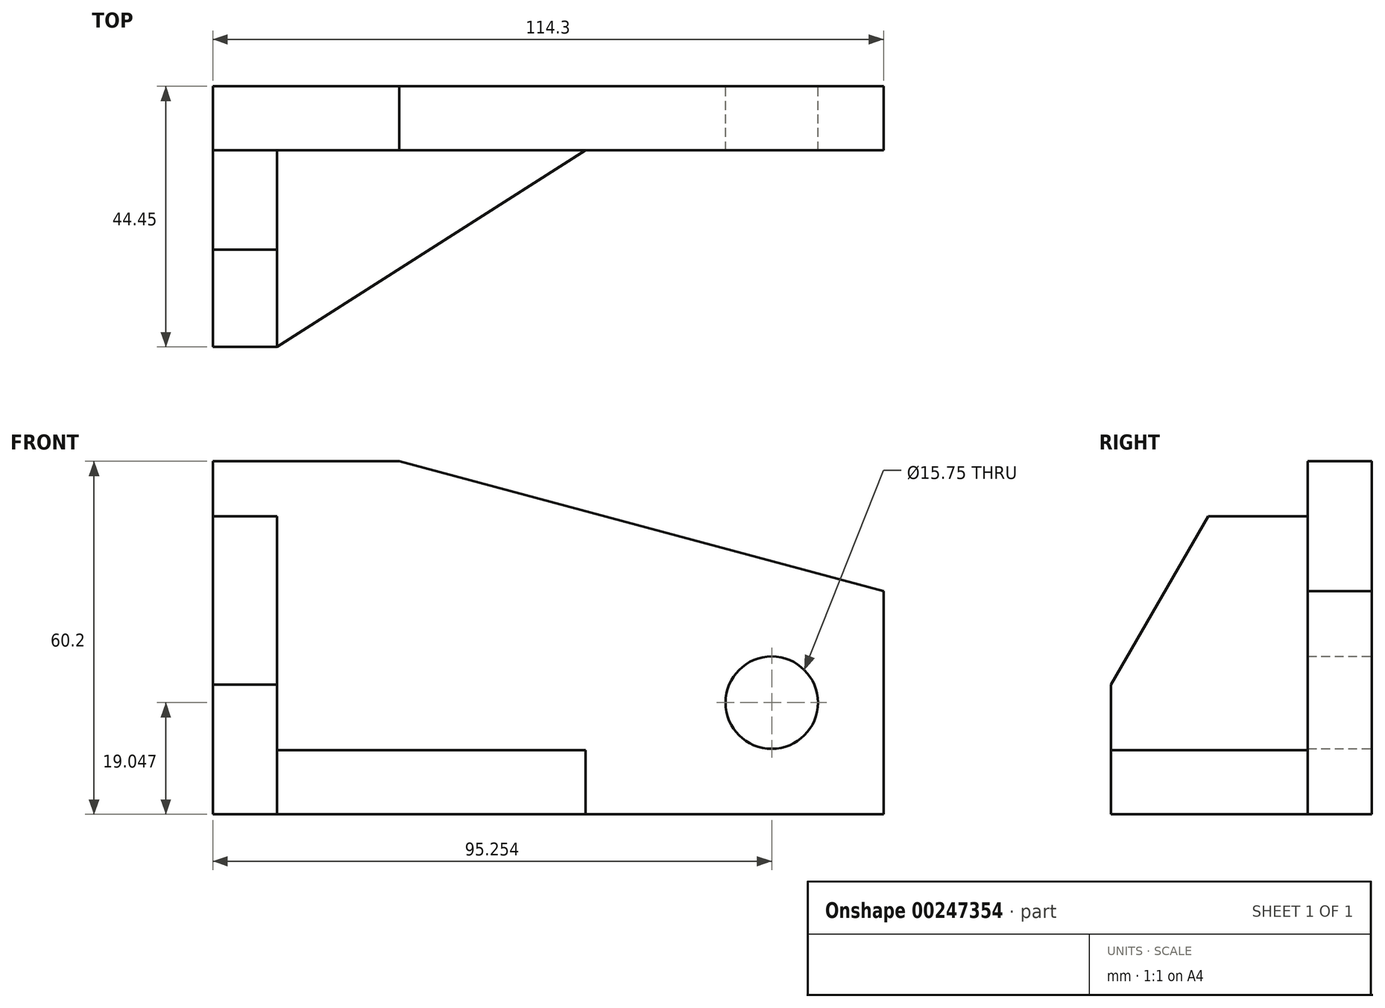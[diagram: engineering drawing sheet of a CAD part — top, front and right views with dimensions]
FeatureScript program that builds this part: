
annotation { "Feature Type Name" : "Feature", "Feature Type Description" : "" }
export const myFeature = defineFeature(function(context is Context, id is Id, definition is map)
    precondition{}
    {
        {
            var Q0;
            Q0=qCreatedBy(makeId("Front.planeOp"),FACE);
            var sketch = newSketch(context, id + "F0", { "sketchPlane" : qUnion([Q0])});
            skLineSegment(sketch, "E0.bottom", {"start": v(-58.6, 2.99) * mm, "end": v(-26.85, 2.99) * mm});
            skLineSegment(sketch, "E0.top", {"start": v(-58.6, -57.21) * mm, "end": v(55.7, -57.21) * mm});
            skLineSegment(sketch, "E0.left", {"start": v(-58.6, 2.99) * mm, "end": v(-58.6, -57.21) * mm});
            skLineSegment(sketch, "E0.right", {"start": v(55.7, -19.13) * mm, "end": v(55.7, -57.21) * mm});
            skLineSegment(sketch, "E1", {"start": v(-26.85, 2.99) * mm, "end": v(55.7, -19.13) * mm});
            skCircle(sketch, "E2", {"center": v(36.65, -38.16) * mm, "radius": 7.87 * mm});
            skSolve(sketch);
        }
        {
            var Q0;
            Q0 = qSketchRegion(id + "F0", true);
            extrude(context, id + "F1", {"entities" : qUnion([Q0]), "depth" : 10.92 * mm});
        }
        {
            var Q0;
            Q0=makeQuery(id+"F1.opExtrude","SWEPT_FACE",FACE,{"disambiguationData":[OSD([sQuery(id+"F0.wireOp",EDGE,"E0.left")])]});
            var sketch = newSketch(context, id + "F2", { "sketchPlane" : qUnion([Q0])});
            skLineSegment(sketch, "E3.bottom", {"start": v(10.92, -57.21) * mm, "end": v(44.45, -57.21) * mm});
            skLineSegment(sketch, "E3.top", {"start": v(10.92, -6.41) * mm, "end": v(27.88, -6.41) * mm});
            skLineSegment(sketch, "E3.left", {"start": v(10.92, -57.21) * mm, "end": v(10.92, -6.41) * mm});
            skLineSegment(sketch, "E3.right", {"start": v(44.45, -57.21) * mm, "end": v(44.45, -35.11) * mm});
            skLineSegment(sketch, "E4", {"start": v(27.88, -6.41) * mm, "end": v(44.45, -35.11) * mm});
            skSolve(sketch);
        }
        {
            var Q0;
            Q0=makeQuery(id+"F2.imprint","IMPRINT",FACE,{"disambiguationData":[TD([[makeQuery(id+"F2.imprint","IMPRINT",EDGE,{"derivedFrom":sQuery(id+"F2.wireOp",EDGE,"E3.bottom")}),1.0]])]});
            extrude(context, id + "F3", {"entities" : qUnion([Q0]), "operationType" : NewBodyOperationType.ADD, "oppositeDirection" : true, "depth" : 10.92 * mm});
        }
        {
            var Q0;
            Q0=makeQuery(id+"F1.opExtrude","SWEPT_FACE",FACE,{"disambiguationData":[OSD([sQuery(id+"F0.wireOp",EDGE,"E0.top")])]});
            var sketch = newSketch(context, id + "F4", { "sketchPlane" : qUnion([Q0])});
            skLineSegment(sketch, "E5.right", {"start": v(-47.67, 10.92) * mm, "end": v(-47.67, 44.45) * mm});
            skLineSegment(sketch, "E6", {"start": v(-47.67, 44.45) * mm, "end": v(4.9, 10.92) * mm});
            skLineSegment(sketch, "E7.0", {"start": v(-26.85, 10.92) * mm, "end": v(55.7, 10.92) * mm});
            skLineSegment(sketch, "E8.0", {"start": v(-58.6, 10.92) * mm, "end": v(-26.85, 10.92) * mm});
            skSolve(sketch);
        }
        {
            var Q0;
            Q0=makeQuery(id+"F4.imprint","IMPRINT",FACE,{"disambiguationData":[TD([[makeQuery(id+"F4.imprint","IMPRINT",EDGE,{"derivedFrom":sQuery(id+"F4.wireOp",EDGE,"E5.bottom")}),1.0]])]});
            var Q1;
            {var subQ0=sQuery(id+"F4.wireOp",EDGE,"E5.right");Q1=makeQuery(id+"F4.imprint","IMPRINT",FACE,{"disambiguationData":[TD([[makeQuery(id+"F4.imprint","IMPRINT",EDGE,{"derivedFrom":subQ0}),-1.0]])]});}
            extrude(context, id + "F5", {"entities" : qUnion([Q0, Q1]), "operationType" : NewBodyOperationType.ADD, "oppositeDirection" : true, "depth" : 10.92 * mm});
        }
    });
